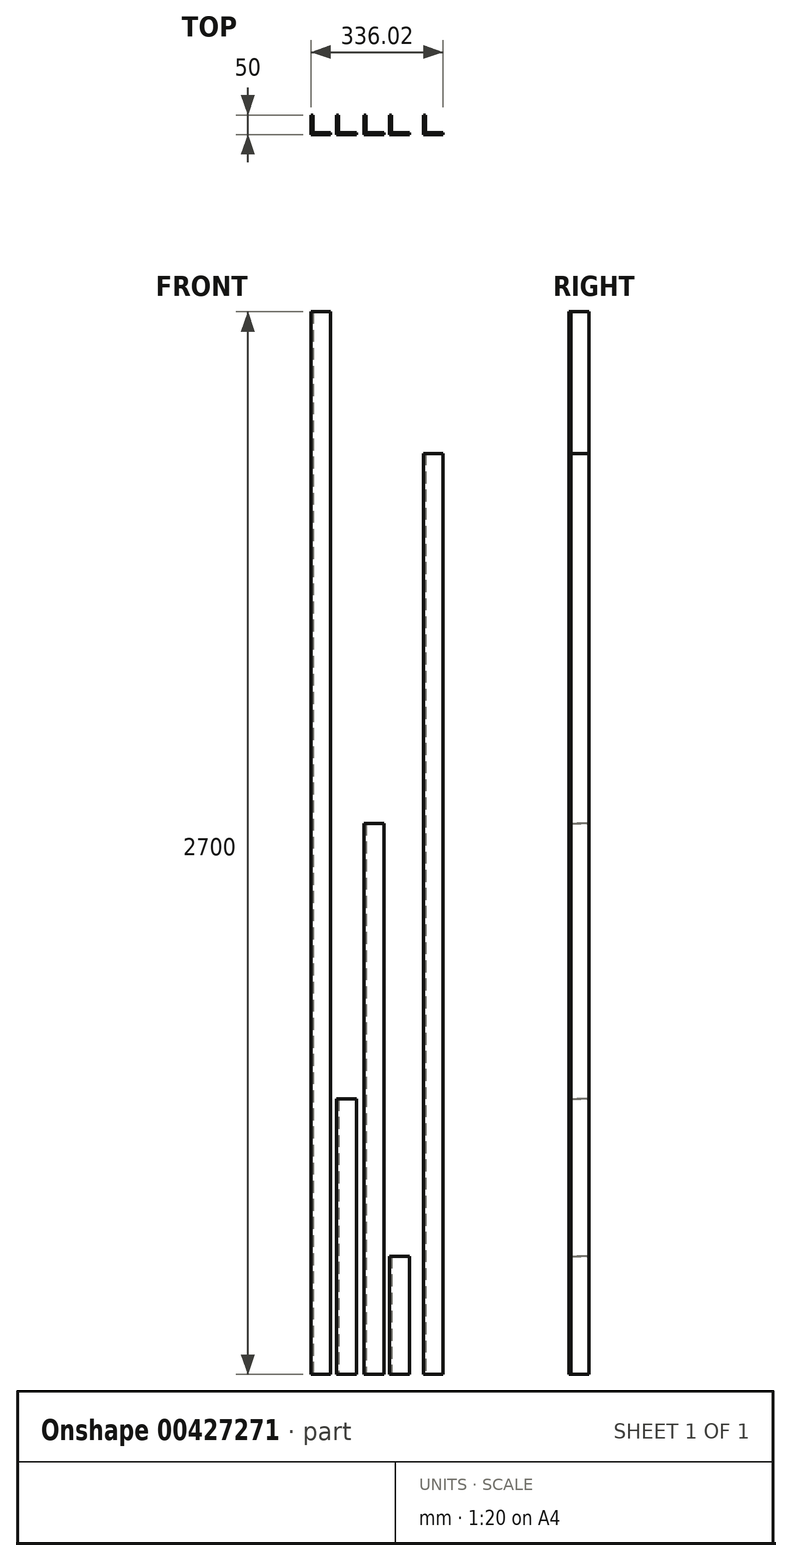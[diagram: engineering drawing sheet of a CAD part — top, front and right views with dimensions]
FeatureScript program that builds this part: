
annotation { "Feature Type Name" : "Feature", "Feature Type Description" : "" }
export const myFeature = defineFeature(function(context is Context, id is Id, definition is map)
    precondition{}
    {
        {
            var Q0;
            Q0=qCreatedBy(makeId("Top.planeOp"),FACE);
            var sketch = newSketch(context, id + "F0", { "sketchPlane" : qUnion([Q0])});
            skLineSegment(sketch, "E0", {"start": v(0, 0) * mm, "end": v(0, 50) * mm});
            skLineSegment(sketch, "E1", {"start": v(0, 50) * mm, "end": v(5, 50) * mm});
            skLineSegment(sketch, "E2", {"start": v(5, 50) * mm, "end": v(5, 5) * mm});
            skLineSegment(sketch, "E3", {"start": v(5, 5) * mm, "end": v(50, 5) * mm});
            skLineSegment(sketch, "E4", {"start": v(50, 5) * mm, "end": v(50, 0) * mm});
            skLineSegment(sketch, "E5", {"start": v(50, 0) * mm, "end": v(0, 0) * mm});
            skSolve(sketch);
        }
        {
            var Q0;
            Q0 = qSketchRegion(id + "F0", true);
            extrude(context, id + "F1", {"entities" : qUnion([Q0]), "depth" : 2700 * mm, "offsetDistance" : 25 * mm});
        }
        {
            var Q0;
            Q0=qCreatedBy(makeId("Top.planeOp"),FACE);
            var sketch = newSketch(context, id + "F2", { "sketchPlane" : qUnion([Q0])});
            skLineSegment(sketch, "E6", {"start": v(65.43, 0) * mm, "end": v(65.43, 50) * mm});
            skLineSegment(sketch, "E7", {"start": v(65.43, 50) * mm, "end": v(70.43, 50) * mm});
            skLineSegment(sketch, "E8", {"start": v(70.43, 50) * mm, "end": v(70.43, 5) * mm});
            skLineSegment(sketch, "E9", {"start": v(70.43, 5) * mm, "end": v(115.43, 5) * mm});
            skLineSegment(sketch, "E10", {"start": v(115.43, 5) * mm, "end": v(115.43, 0) * mm});
            skLineSegment(sketch, "E11", {"start": v(115.43, 0) * mm, "end": v(65.43, 0) * mm});
            skSolve(sketch);
        }
        {
            var Q0;
            Q0 = qSketchRegion(id + "F2", true);
            extrude(context, id + "F3", {"entities" : qUnion([Q0]), "depth" : 700 * mm, "offsetDistance" : 25 * mm});
        }
        {
            var Q0;
            Q0=qCreatedBy(makeId("Top.planeOp"),FACE);
            var sketch = newSketch(context, id + "F4", { "sketchPlane" : qUnion([Q0])});
            skLineSegment(sketch, "E12", {"start": v(135.33, 0) * mm, "end": v(135.33, 50) * mm});
            skLineSegment(sketch, "E13", {"start": v(135.33, 50) * mm, "end": v(140.33, 50) * mm});
            skLineSegment(sketch, "E14", {"start": v(140.33, 50) * mm, "end": v(140.33, 5) * mm});
            skLineSegment(sketch, "E15", {"start": v(140.33, 5) * mm, "end": v(185.33, 5) * mm});
            skLineSegment(sketch, "E16", {"start": v(185.33, 5) * mm, "end": v(185.33, 0) * mm});
            skLineSegment(sketch, "E17", {"start": v(185.33, 0) * mm, "end": v(135.33, 0) * mm});
            skSolve(sketch);
        }
        {
            var Q0;
            Q0=qCreatedBy(makeId("Top.planeOp"),FACE);
            var sketch = newSketch(context, id + "F5", { "sketchPlane" : qUnion([Q0])});
            skLineSegment(sketch, "E18", {"start": v(200.4, 0) * mm, "end": v(200.4, 50) * mm});
            skLineSegment(sketch, "E19", {"start": v(200.4, 50) * mm, "end": v(205.4, 50) * mm});
            skLineSegment(sketch, "E20", {"start": v(205.4, 50) * mm, "end": v(205.4, 5) * mm});
            skLineSegment(sketch, "E21", {"start": v(205.4, 5) * mm, "end": v(250.4, 5) * mm});
            skLineSegment(sketch, "E22", {"start": v(250.4, 5) * mm, "end": v(250.4, 0) * mm});
            skLineSegment(sketch, "E23", {"start": v(250.4, 0) * mm, "end": v(200.4, 0) * mm});
            skSolve(sketch);
        }
        {
            var Q0;
            Q0 = qSketchRegion(id + "F4", true);
            extrude(context, id + "F6", {"entities" : qUnion([Q0]), "depth" : 1400 * mm, "offsetDistance" : 25 * mm});
        }
        {
            var Q0;
            Q0 = qSketchRegion(id + "F5", true);
            extrude(context, id + "F7", {"entities" : qUnion([Q0]), "depth" : 300 * mm, "offsetDistance" : 25 * mm});
        }
        {
            var Q0;
            Q0=qCreatedBy(makeId("Top.planeOp"),FACE);
            var sketch = newSketch(context, id + "F8", { "sketchPlane" : qUnion([Q0])});
            skLineSegment(sketch, "E24", {"start": v(286.02, 0) * mm, "end": v(286.02, 50) * mm});
            skLineSegment(sketch, "E25", {"start": v(286.02, 50) * mm, "end": v(291.02, 50) * mm});
            skLineSegment(sketch, "E26", {"start": v(291.02, 50) * mm, "end": v(291.02, 5) * mm});
            skLineSegment(sketch, "E27", {"start": v(291.02, 5) * mm, "end": v(336.02, 5) * mm});
            skLineSegment(sketch, "E28", {"start": v(336.02, 5) * mm, "end": v(336.02, 0) * mm});
            skLineSegment(sketch, "E29", {"start": v(336.02, 0) * mm, "end": v(286.02, 0) * mm});
            skSolve(sketch);
        }
        {
            var Q0;
            Q0 = qSketchRegion(id + "F8", true);
            extrude(context, id + "F9", {"entities" : qUnion([Q0]), "depth" : 2340 * mm, "offsetDistance" : 25 * mm});
        }
    });
